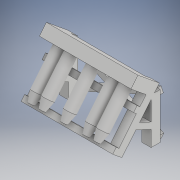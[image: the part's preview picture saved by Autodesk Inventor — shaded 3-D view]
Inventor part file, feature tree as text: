
AUTODESK INVENTOR PART (.ipt)
format: ipt  version: 2019 (Build 230136000, 136)  size: 280,576 bytes
history: native  units: mm
features: sketch x15, extrude x14, mirror x8, plane x5, loft x1, other x1
ambient origin geometry x8: Origin, YZ Plane, XZ Plane, XY Plane, X Axis, Y Axis, Z Axis, Center Point
bodies: Solid1 (feature_tree)
feature tree (44):
  extrude  "Extrusion1"  Depth=50.0mm
  extrude  "Extrusion2"  Depth=50.0mm
  extrude  "Extrusion3"  Depth=20.0mm TaperAngle=0.0deg
  extrude  "Extrusion4"  Depth=50.0mm TaperAngle=0.0deg
  extrude  "Extrusion5"  Depth=400.0mm
  extrude  "Extrusion6"  Depth=30.0mm
  extrude  "Extrusion7"  Depth=30.0mm
  extrude  "Extrusion8"  Depth=60.0mm
  extrude  "Extrusion9"  Depth=500.0mm TaperAngle=0.0deg
  extrude  "Extrusion10"  Depth=500.0mm TaperAngle=0.0deg
  extrude  "Extrusion11"  Depth=30.0mm
  plane  "Work Plane1"
  loft  "Loft1"
  plane  "Work Plane2"
  mirror  "Mirror1"
  mirror  "Mirror2"
  plane  "Work Plane3"
  mirror  "Mirror5"
  mirror  "Mirror6"
  extrude  "Extrusion13"  [1 undecoded]
  extrude  "Extrusion14"  Depth=500.0mm TaperAngle=0.0deg
  plane  "Work Plane5"
  mirror  "Mirror7"
  mirror  "Mirror8"
  plane  "Work Plane6"
  mirror  "Mirror9"
  mirror  "Mirror10"
  extrude  "Extrusion15"  [1 undecoded]
  sketch  "Sketch1"  dims[d0=250.0mm d1=50.0mm]
  sketch  "Sketch2"  dims[d2=250.0mm d3=50.0mm]
  sketch  "Sketch3"  dims[d4=50.0mm d5=0.0mm d6=20.0mm d7=0.0mm]
  sketch  "Sketch4"  dims[d8=500.0mm d9=0.0mm d10=50.0mm d11=0.0mm]
  sketch  "Sketch5"  dims[d12=50.0mm d13=0.0mm d14=400.0mm]
  sketch  "Sketch7"  dims[d15=50.0mm d16=0.0mm d17=30.0mm]
  sketch  "Sketch8"  dims[d18=20.0mm d19=0.0mm d20=30.0mm]
  sketch  "Sketch9"  dims[d21=20.0mm d22=0.0mm d23=60.0mm]
  sketch  "Sketch10"  dims[d24=500.0mm d25=0.0mm d26=200.0mm d27=0.0mm]
  sketch  "Sketch11"  dims[d28=60.0mm d29=500.0mm d30=0.0mm]
  sketch  "Sketch12"  dims[d31=50.0mm d32=30.0mm]
  sketch  "Sketch14"  dims[d33=0.0mm d34=90.0deg d35=0.0mm d36=90.0deg]
  other  "Edges1"
  sketch  "Sketch17"  dims[d37=-190.0mm d38=-100.0mm]
  sketch  "Sketch18"  dims[d41=500.0mm d42=0.0mm d43=500.0mm d44=0.0mm]
  sketch  "Sketch19"  dims[d45=-190.0mm d46=-100.0mm d47=500.0mm d48=0.0mm]
note: 2 required parameter values undecoded (feature->parameter linkage not recoverable at this tier; creation-order binding heuristic only, values carry confidence <= 0.55)
